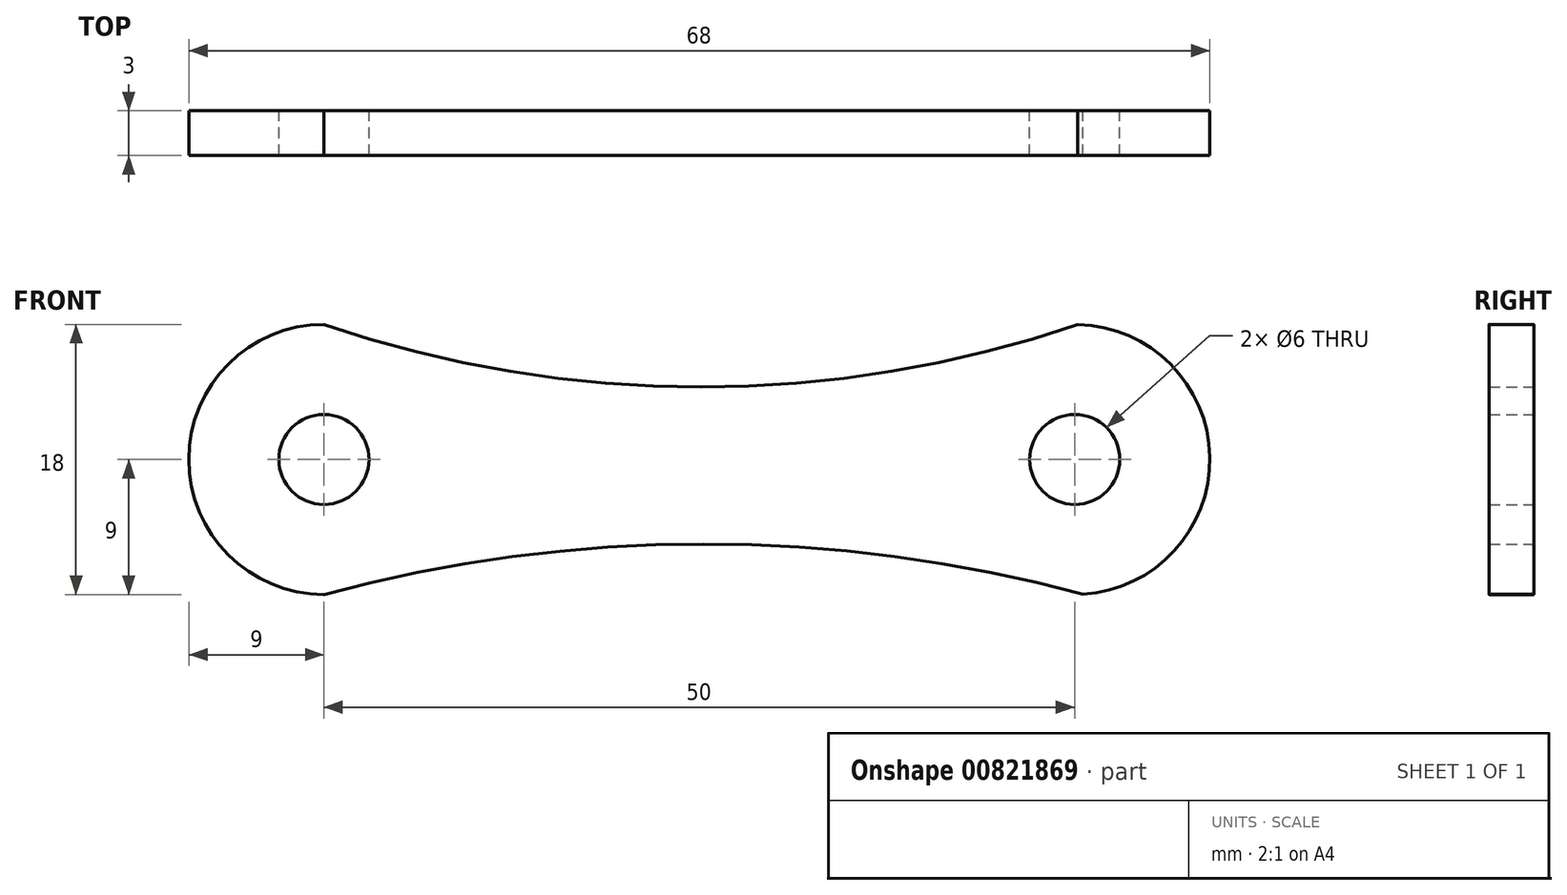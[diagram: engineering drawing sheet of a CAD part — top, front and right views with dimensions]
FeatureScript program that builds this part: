
annotation { "Feature Type Name" : "Feature", "Feature Type Description" : "" }
export const myFeature = defineFeature(function(context is Context, id is Id, definition is map)
    precondition{}
    {
        {
            var Q0;
            Q0=qCreatedBy(makeId("Front.planeOp"),FACE);
            var sketch = newSketch(context, id + "F0", { "sketchPlane" : qUnion([Q0])});
            skCircle(sketch, "E0", {"center": v(0, 0) * mm, "radius": 3 * mm});
            skCircle(sketch, "E1", {"center": v(0, 0) * mm, "radius": 9 * mm});
            skCircle(sketch, "E2", {"center": v(50, 0) * mm, "radius": 3 * mm});
            skCircle(sketch, "E3", {"center": v(50, 0) * mm, "radius": 9 * mm});
            skArc(sketch, "E4", {"start": v(0, 9) * mm, "mid": v(25.1, 4.82) * mm, "end": v(50.21, 9) * mm});
            skArc(sketch, "E5", {"start": v(50.56, -8.98) * mm, "mid": v(25.28, -5.63) * mm, "end": v(0, -9) * mm});
            skSolve(sketch);
        }
        {
            var Q0;
            Q0=makeQuery(id+"F0.imprint","IMPRINT",FACE,{"disambiguationData":[TD([[makeQuery(id+"F0.imprint","IMPRINT",EDGE,{"derivedFrom":sQuery(id+"F0.wireOp",EDGE,"E0")}),-1.0]])]});
            var Q1;
            {var subQ0=sQuery(id+"F0.wireOp",EDGE,"E4");var subQ1=sQuery(id+"F0.wireOp",EDGE,"E1");var subQ2=makeQuery(id+"F0.imprint","INTERSECT",VERTEX,{"disambiguationData":[OD(1.0)],"derivedFrom":[subQ1,subQ0]});Q1=makeQuery(id+"F0.imprint","IMPRINT",FACE,{"disambiguationData":[TD([[makeQuery(id+"F0.imprint","IMPRINT",EDGE,{"disambiguationData":[TD([[subQ2,1.0]])],"derivedFrom":subQ1}),-1.0]])]});}
            var Q2;
            Q2=makeQuery(id+"F0.imprint","IMPRINT",FACE,{"disambiguationData":[TD([[makeQuery(id+"F0.imprint","IMPRINT",EDGE,{"derivedFrom":sQuery(id+"F0.wireOp",EDGE,"E2")}),-1.0]])]});
            extrude(context, id + "F1", {"entities" : qUnion([Q0, Q1, Q2]), "depth" : 3 * mm, "offsetDistance" : 25 * mm});
        }
    });
